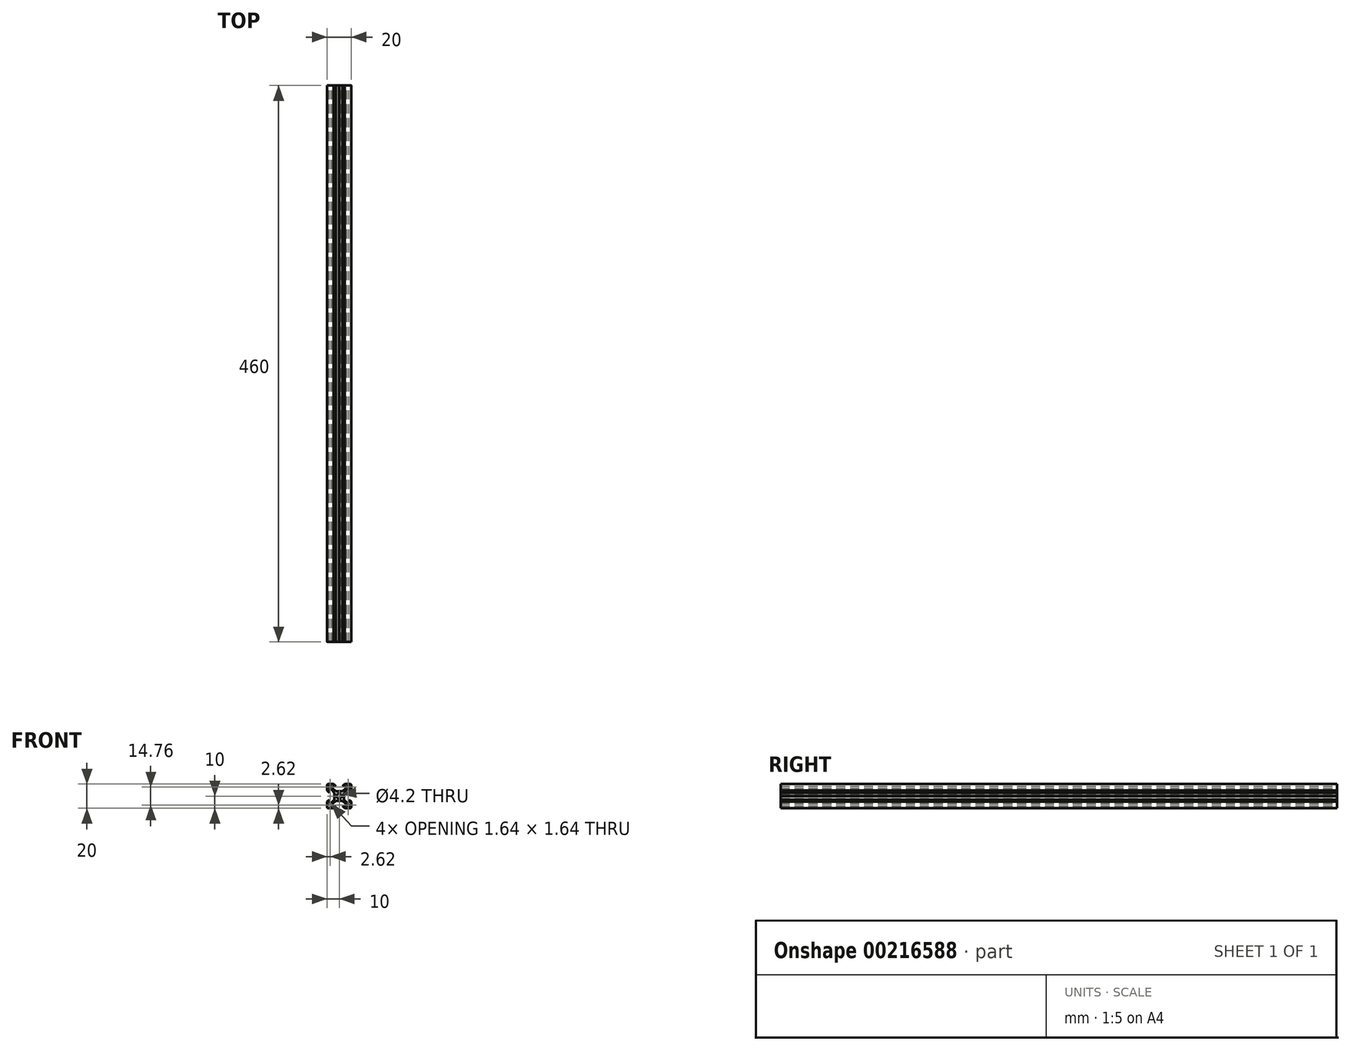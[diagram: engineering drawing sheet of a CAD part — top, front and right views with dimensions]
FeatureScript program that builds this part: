
annotation { "Feature Type Name" : "Feature", "Feature Type Description" : "" }
export const myFeature = defineFeature(function(context is Context, id is Id, definition is map)
    precondition{}
    {
        {
            var Q0;
            Q0=qCreatedBy(makeId("Front.planeOp"),FACE);
            var sketch = newSketch(context, id + "F0", { "sketchPlane" : qUnion([Q0])});
            skLineSegment(sketch, "E0.rect.bottom", {"start": v(-9, 10) * mm, "end": v(9, 10) * mm});
            skLineSegment(sketch, "E0.rect.top", {"start": v(-9, -10) * mm, "end": v(9, -10) * mm});
            skLineSegment(sketch, "E0.rect.left", {"start": v(-10, 9) * mm, "end": v(-10, -9) * mm});
            skLineSegment(sketch, "E0.rect.right", {"start": v(10, 9) * mm, "end": v(10, -9) * mm});
            skPoint(sketch, "E0.rect.middle", {"position": v(0, 0) * mm});
            skCircle(sketch, "E1", {"center": v(0, 0) * mm, "radius": 2.1 * mm});
            skPoint(sketch, "E2.visualSharp", {"position": v(-10, 10) * mm});
            skArc(sketch, "E2.filletArc", {"start": v(-9, 10) * mm, "mid": v(-9.7, 9.7) * mm, "end": v(-10, 9) * mm});
            skPoint(sketch, "E3.visualSharp", {"position": v(10, 10) * mm});
            skArc(sketch, "E3.filletArc", {"start": v(10, 9) * mm, "mid": v(9.7, 9.7) * mm, "end": v(9, 10) * mm});
            skPoint(sketch, "E4.visualSharp", {"position": v(10, -10) * mm});
            skArc(sketch, "E4.filletArc", {"start": v(9, -10) * mm, "mid": v(9.7, -9.7) * mm, "end": v(10, -9) * mm});
            skPoint(sketch, "E5.visualSharp", {"position": v(-10, -10) * mm});
            skArc(sketch, "E5.filletArc", {"start": v(-10, -9) * mm, "mid": v(-9.7, -9.7) * mm, "end": v(-9, -10) * mm});
            skLineSegment(sketch, "E6", {"start": v(10, 10) * mm, "end": v(-10, -10) * mm, "construction": true});
            skLineSegment(sketch, "E7", {"start": v(-10, 10) * mm, "end": v(10, -10) * mm, "construction": true});
            skLineSegment(sketch, "E8", {"start": v(-4.64, 10) * mm, "end": v(-2.84, 8.2) * mm});
            skLineSegment(sketch, "E9", {"start": v(-2.84, 8.2) * mm, "end": v(-5.5, 8.2) * mm});
            skLineSegment(sketch, "E10", {"start": v(-5.5, 8.2) * mm, "end": v(-5.5, 6.56) * mm});
            skLineSegment(sketch, "E11", {"start": v(-5.5, 6.56) * mm, "end": v(-2.84, 3.9) * mm});
            skLineSegment(sketch, "E12.MirrorCS", {"start": v(4.64, 10) * mm, "end": v(2.84, 8.2) * mm});
            skLineSegment(sketch, "E13.MirrorCS", {"start": v(2.84, 8.2) * mm, "end": v(5.5, 8.2) * mm});
            skLineSegment(sketch, "E14.MirrorCS", {"start": v(5.5, 8.2) * mm, "end": v(5.5, 6.56) * mm});
            skLineSegment(sketch, "E15.MirrorCS", {"start": v(5.5, 6.56) * mm, "end": v(2.84, 3.9) * mm});
            skLineSegment(sketch, "E16", {"start": v(-2.84, 3.9) * mm, "end": v(2.84, 3.9) * mm});
            skLineSegment(sketch, "E17.MirrorCS", {"start": v(-4.64, -10) * mm, "end": v(-2.84, -8.2) * mm});
            skLineSegment(sketch, "E18.MirrorCS", {"start": v(-2.84, -8.2) * mm, "end": v(-5.5, -8.2) * mm});
            skLineSegment(sketch, "E19.MirrorCS", {"start": v(-5.5, -8.2) * mm, "end": v(-5.5, -6.56) * mm});
            skLineSegment(sketch, "E20.MirrorCS", {"start": v(-5.5, -6.56) * mm, "end": v(-2.84, -3.9) * mm});
            skLineSegment(sketch, "E21.MirrorCS", {"start": v(-2.84, -3.9) * mm, "end": v(2.84, -3.9) * mm});
            skLineSegment(sketch, "E22.MirrorCS", {"start": v(5.5, -6.56) * mm, "end": v(2.84, -3.9) * mm});
            skLineSegment(sketch, "E23.MirrorCS", {"start": v(5.5, -8.2) * mm, "end": v(5.5, -6.56) * mm});
            skLineSegment(sketch, "E24.MirrorCS", {"start": v(2.84, -8.2) * mm, "end": v(5.5, -8.2) * mm});
            skLineSegment(sketch, "E25.MirrorCS", {"start": v(4.64, -10) * mm, "end": v(2.84, -8.2) * mm});
            skLineSegment(sketch, "E26.MirrorCS", {"start": v(10, -4.64) * mm, "end": v(8.2, -2.84) * mm});
            skLineSegment(sketch, "E27.MirrorCS", {"start": v(8.2, -2.84) * mm, "end": v(8.2, -5.5) * mm});
            skLineSegment(sketch, "E28.MirrorCS", {"start": v(8.2, -5.5) * mm, "end": v(6.56, -5.5) * mm});
            skLineSegment(sketch, "E29.MirrorCS", {"start": v(6.56, -5.5) * mm, "end": v(3.9, -2.84) * mm});
            skLineSegment(sketch, "E30.MirrorCS", {"start": v(3.9, -2.84) * mm, "end": v(3.9, 2.84) * mm});
            skLineSegment(sketch, "E31.MirrorCS", {"start": v(6.56, 5.5) * mm, "end": v(3.9, 2.84) * mm});
            skLineSegment(sketch, "E32.MirrorCS", {"start": v(8.2, 5.5) * mm, "end": v(6.56, 5.5) * mm});
            skLineSegment(sketch, "E33.MirrorCS", {"start": v(8.2, 2.84) * mm, "end": v(8.2, 5.5) * mm});
            skLineSegment(sketch, "E34.MirrorCS", {"start": v(10, 4.64) * mm, "end": v(8.2, 2.84) * mm});
            skLineSegment(sketch, "E35.MirrorCS", {"start": v(-8.2, 2.84) * mm, "end": v(-8.2, 5.5) * mm});
            skLineSegment(sketch, "E36.MirrorCS", {"start": v(-10, 4.64) * mm, "end": v(-8.2, 2.84) * mm});
            skLineSegment(sketch, "E37.MirrorCS", {"start": v(-8.2, 5.5) * mm, "end": v(-6.56, 5.5) * mm});
            skLineSegment(sketch, "E38.MirrorCS", {"start": v(-6.56, 5.5) * mm, "end": v(-3.9, 2.84) * mm});
            skLineSegment(sketch, "E39.MirrorCS", {"start": v(-3.9, 2.84) * mm, "end": v(-3.9, -2.84) * mm});
            skLineSegment(sketch, "E40.MirrorCS", {"start": v(-6.56, -5.5) * mm, "end": v(-3.9, -2.84) * mm});
            skLineSegment(sketch, "E41.MirrorCS", {"start": v(-8.2, -5.5) * mm, "end": v(-6.56, -5.5) * mm});
            skLineSegment(sketch, "E42.MirrorCS", {"start": v(-8.2, -2.84) * mm, "end": v(-8.2, -5.5) * mm});
            skLineSegment(sketch, "E43.MirrorCS", {"start": v(-10, -4.64) * mm, "end": v(-8.2, -2.84) * mm});
            skLineSegment(sketch, "E44", {"start": v(-8.05, 8.2) * mm, "end": v(-6.71, 8.2) * mm});
            skLineSegment(sketch, "E45", {"start": v(-6.56, 8.05) * mm, "end": v(-6.56, 8.05) * mm});
            skLineSegment(sketch, "E46", {"start": v(-6.6, 7.94) * mm, "end": v(-7.94, 6.6) * mm});
            skLineSegment(sketch, "E47", {"start": v(-8.05, 6.56) * mm, "end": v(-8.05, 6.56) * mm});
            skLineSegment(sketch, "E48", {"start": v(-8.2, 6.7) * mm, "end": v(-8.2, 8.05) * mm});
            skLineSegment(sketch, "E49.MirrorCS", {"start": v(8.2, 6.71) * mm, "end": v(8.2, 8.05) * mm});
            skLineSegment(sketch, "E50.MirrorCS", {"start": v(7.99, 6.56) * mm, "end": v(8.05, 6.56) * mm});
            skLineSegment(sketch, "E51.MirrorCS", {"start": v(6.56, 7.99) * mm, "end": v(7.99, 6.56) * mm});
            skLineSegment(sketch, "E52.MirrorCS", {"start": v(6.56, 8.05) * mm, "end": v(6.56, 7.99) * mm});
            skLineSegment(sketch, "E53.MirrorCS", {"start": v(8.05, 8.2) * mm, "end": v(6.7, 8.2) * mm});
            skLineSegment(sketch, "E54.MirrorCS", {"start": v(-8.2, -6.7) * mm, "end": v(-8.2, -8.2) * mm});
            skLineSegment(sketch, "E55.MirrorCS", {"start": v(-7.99, -6.56) * mm, "end": v(-8.05, -6.56) * mm});
            skLineSegment(sketch, "E56.MirrorCS", {"start": v(-6.6, -7.94) * mm, "end": v(-7.99, -6.56) * mm});
            skLineSegment(sketch, "E57.MirrorCS", {"start": v(-6.56, -8.05) * mm, "end": v(-6.56, -8.05) * mm});
            skLineSegment(sketch, "E58.MirrorCS", {"start": v(-8.2, -8.2) * mm, "end": v(-6.7, -8.2) * mm});
            skLineSegment(sketch, "E59.MirrorCS", {"start": v(6.56, -8.05) * mm, "end": v(6.56, -7.99) * mm});
            skLineSegment(sketch, "E60.MirrorCS", {"start": v(6.56, -7.99) * mm, "end": v(7.94, -6.6) * mm});
            skLineSegment(sketch, "E61.MirrorCS", {"start": v(8.05, -6.56) * mm, "end": v(8.2, -6.56) * mm});
            skLineSegment(sketch, "E62.MirrorCS", {"start": v(8.2, -6.56) * mm, "end": v(8.2, -8.05) * mm});
            skLineSegment(sketch, "E63.MirrorCS", {"start": v(8.05, -8.2) * mm, "end": v(6.7, -8.2) * mm});
            skLineSegment(sketch, "E64", {"start": v(-0.15, 3.9) * mm, "end": v(0, 3.75) * mm});
            skLineSegment(sketch, "E65", {"start": v(0, 3.75) * mm, "end": v(0.15, 3.9) * mm});
            skLineSegment(sketch, "E66.MirrorCS", {"start": v(-0.15, -3.9) * mm, "end": v(0, -3.75) * mm});
            skLineSegment(sketch, "E67.MirrorCS", {"start": v(0, -3.75) * mm, "end": v(0.15, -3.9) * mm});
            skLineSegment(sketch, "E68.MirrorCS", {"start": v(3.9, -0.15) * mm, "end": v(3.75, 0) * mm});
            skLineSegment(sketch, "E69.MirrorCS", {"start": v(3.75, 0) * mm, "end": v(3.9, 0.15) * mm});
            skLineSegment(sketch, "E70.MirrorCS", {"start": v(-3.9, 0.15) * mm, "end": v(-3.75, 0) * mm});
            skLineSegment(sketch, "E71.MirrorCS", {"start": v(-3.75, 0) * mm, "end": v(-3.9, -0.15) * mm});
            skPoint(sketch, "E72.visualSharp", {"position": v(-8.2, 8.2) * mm});
            skArc(sketch, "E72.filletArc", {"start": v(-8.05, 8.2) * mm, "mid": v(-8.16, 8.16) * mm, "end": v(-8.2, 8.05) * mm});
            skPoint(sketch, "E73.visualSharp", {"position": v(-6.56, 7.99) * mm});
            skArc(sketch, "E73.filletArc", {"start": v(-6.6, 7.94) * mm, "mid": v(-6.57, 8) * mm, "end": v(-6.56, 8.05) * mm});
            skPoint(sketch, "E74.visualSharp", {"position": v(-7.99, 6.56) * mm});
            skArc(sketch, "E74.filletArc", {"start": v(-8.05, 6.56) * mm, "mid": v(-8, 6.57) * mm, "end": v(-7.94, 6.6) * mm});
            skPoint(sketch, "E75.visualSharp", {"position": v(-6.56, 8.2) * mm});
            skArc(sketch, "E75.filletArc", {"start": v(-6.56, 8.05) * mm, "mid": v(-6.6, 8.16) * mm, "end": v(-6.71, 8.2) * mm});
            skPoint(sketch, "E76.visualSharp", {"position": v(-8.2, 6.56) * mm});
            skArc(sketch, "E76.filletArc", {"start": v(-8.2, 6.7) * mm, "mid": v(-8.16, 6.6) * mm, "end": v(-8.05, 6.56) * mm});
            skPoint(sketch, "E77.visualSharp", {"position": v(6.56, 8.2) * mm});
            skArc(sketch, "E77.filletArc", {"start": v(6.7, 8.2) * mm, "mid": v(6.6, 8.16) * mm, "end": v(6.56, 8.05) * mm});
            skPoint(sketch, "E78.visualSharp", {"position": v(8.2, 8.2) * mm});
            skArc(sketch, "E78.filletArc", {"start": v(8.2, 8.05) * mm, "mid": v(8.16, 8.16) * mm, "end": v(8.05, 8.2) * mm});
            skPoint(sketch, "E79.visualSharp", {"position": v(8.2, 6.56) * mm});
            skArc(sketch, "E79.filletArc", {"start": v(8.05, 6.56) * mm, "mid": v(8.16, 6.6) * mm, "end": v(8.2, 6.71) * mm});
            skPoint(sketch, "E80.visualSharp", {"position": v(6.56, -8.2) * mm});
            skArc(sketch, "E80.filletArc", {"start": v(6.56, -8.05) * mm, "mid": v(6.6, -8.16) * mm, "end": v(6.7, -8.2) * mm});
            skPoint(sketch, "E81.visualSharp", {"position": v(7.99, -6.56) * mm});
            skArc(sketch, "E81.filletArc", {"start": v(8.05, -6.56) * mm, "mid": v(8, -6.57) * mm, "end": v(7.94, -6.6) * mm});
            skPoint(sketch, "E82.visualSharp", {"position": v(8.2, -8.2) * mm});
            skArc(sketch, "E82.filletArc", {"start": v(8.05, -8.2) * mm, "mid": v(8.16, -8.16) * mm, "end": v(8.2, -8.05) * mm});
            skPoint(sketch, "E83.visualSharp", {"position": v(-6.56, -8.2) * mm});
            skArc(sketch, "E83.filletArc", {"start": v(-6.7, -8.2) * mm, "mid": v(-6.6, -8.16) * mm, "end": v(-6.56, -8.05) * mm});
            skPoint(sketch, "E84.visualSharp", {"position": v(-8.2, -6.56) * mm});
            skArc(sketch, "E84.filletArc", {"start": v(-8.05, -6.56) * mm, "mid": v(-8.16, -6.6) * mm, "end": v(-8.2, -6.7) * mm});
            skPoint(sketch, "E85.visualSharp", {"position": v(-6.56, -7.99) * mm});
            skArc(sketch, "E85.filletArc", {"start": v(-6.56, -8.05) * mm, "mid": v(-6.57, -8) * mm, "end": v(-6.6, -7.94) * mm});
            skSolve(sketch);
        }
        {
            var Q0;
            Q0=makeQuery(id+"F0.imprint","IMPRINT",FACE,{"disambiguationData":[TD([[makeQuery(id+"F0.imprint","IMPRINT",EDGE,{"derivedFrom":sQuery(id+"F0.wireOp",EDGE,"E1")}),-1.0]])]});
            extrude(context, id + "F1", {"entities" : qUnion([Q0]), "depth" : 460 * mm});
        }
    });
